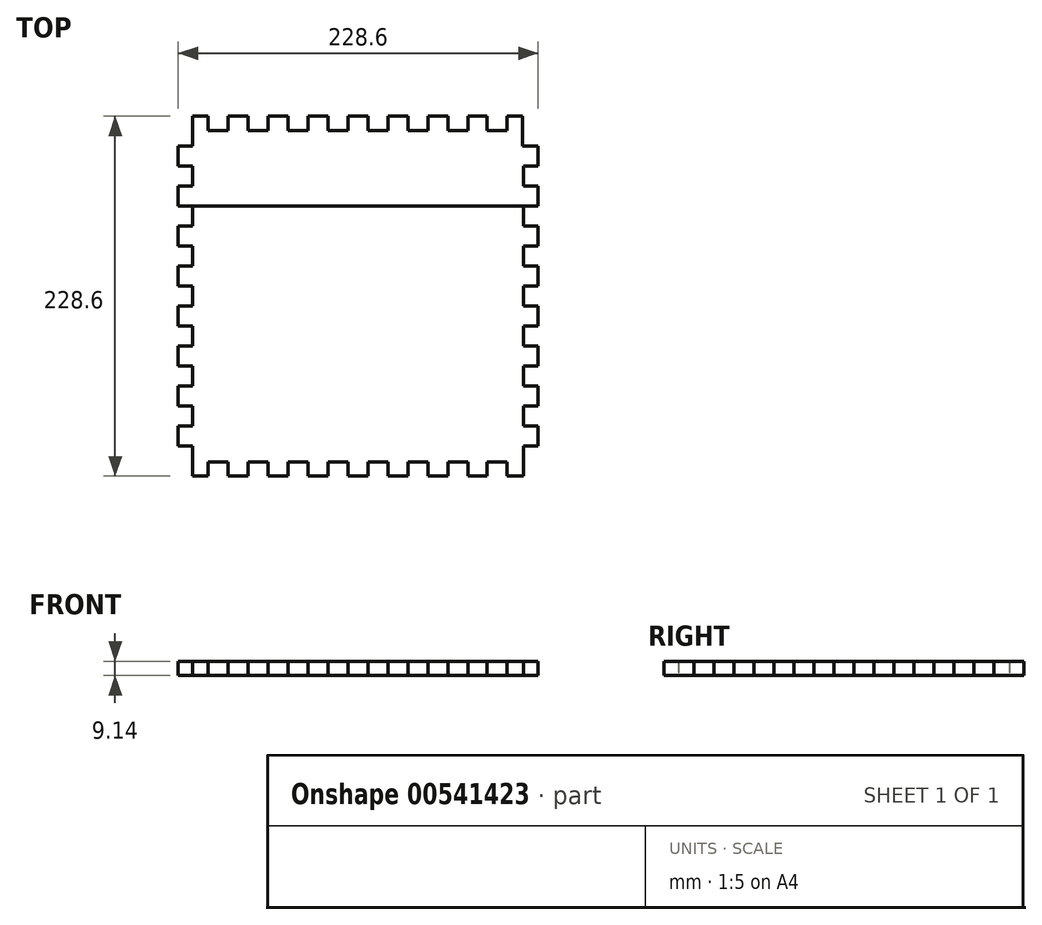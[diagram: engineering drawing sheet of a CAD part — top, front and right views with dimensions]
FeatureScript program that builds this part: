
annotation { "Feature Type Name" : "Feature", "Feature Type Description" : "" }
export const myFeature = defineFeature(function(context is Context, id is Id, definition is map)
    precondition{}
    {
        {
            var Q0;
            Q0=qCreatedBy(makeId("Top.planeOp"),FACE);
            var sketch = newSketch(context, id + "F0", { "sketchPlane" : qUnion([Q0])});
            skLineSegment(sketch, "E0.bottom", {"start": v(9.14, 0) * mm, "end": v(19.05, 0) * mm});
            skLineSegment(sketch, "E0.left", {"start": v(0, -19.05) * mm, "end": v(0, -31.75) * mm});
            skLineSegment(sketch, "E1", {"start": v(9.14, 0) * mm, "end": v(9.14, -19.05) * mm});
            skLineSegment(sketch, "E2", {"start": v(9.14, -19.05) * mm, "end": v(0, -19.05) * mm});
            skPoint(sketch, "E3.orphan", {"position": v(0, 0) * mm});
            skLineSegment(sketch, "E4", {"start": v(19.05, 0) * mm, "end": v(19.05, -9.14) * mm});
            skLineSegment(sketch, "E5", {"start": v(19.05, -9.14) * mm, "end": v(31.75, -9.14) * mm});
            skLineSegment(sketch, "E6", {"start": v(31.75, -9.14) * mm, "end": v(31.75, 0) * mm});
            skLineSegment(sketch, "E7", {"start": v(31.75, 0) * mm, "end": v(44.45, 0) * mm});
            skLineSegment(sketch, "E8", {"start": v(44.45, 0) * mm, "end": v(44.45, -9.14) * mm});
            skLineSegment(sketch, "E9", {"start": v(44.45, -9.14) * mm, "end": v(57.15, -9.14) * mm});
            skLineSegment(sketch, "E10", {"start": v(57.15, -9.14) * mm, "end": v(57.15, 0) * mm});
            skLineSegment(sketch, "E11", {"start": v(57.15, 0) * mm, "end": v(69.85, 0) * mm});
            skLineSegment(sketch, "E12", {"start": v(69.85, 0) * mm, "end": v(69.85, -9.14) * mm});
            skLineSegment(sketch, "E13", {"start": v(69.85, -9.14) * mm, "end": v(82.55, -9.14) * mm});
            skLineSegment(sketch, "E14", {"start": v(82.55, -9.14) * mm, "end": v(82.55, 0) * mm});
            skLineSegment(sketch, "E15", {"start": v(82.55, 0) * mm, "end": v(95.25, 0) * mm});
            skLineSegment(sketch, "E16", {"start": v(95.25, 0) * mm, "end": v(95.25, -9.14) * mm});
            skLineSegment(sketch, "E17", {"start": v(95.25, -9.14) * mm, "end": v(107.95, -9.14) * mm});
            skLineSegment(sketch, "E18", {"start": v(107.95, -9.14) * mm, "end": v(107.95, 0) * mm});
            skLineSegment(sketch, "E19.trimOffspring", {"start": v(107.95, 0) * mm, "end": v(120.65, 0) * mm});
            skLineSegment(sketch, "E20", {"start": v(120.65, 0) * mm, "end": v(120.65, -9.14) * mm});
            skLineSegment(sketch, "E21", {"start": v(120.65, -9.14) * mm, "end": v(133.35, -9.14) * mm});
            skLineSegment(sketch, "E22", {"start": v(133.35, -9.14) * mm, "end": v(133.35, 0) * mm});
            skLineSegment(sketch, "E23", {"start": v(133.35, 0) * mm, "end": v(146.05, 0) * mm});
            skLineSegment(sketch, "E24", {"start": v(146.05, 0) * mm, "end": v(146.05, -9.14) * mm});
            skLineSegment(sketch, "E25", {"start": v(146.05, -9.14) * mm, "end": v(158.75, -9.14) * mm});
            skLineSegment(sketch, "E26", {"start": v(158.75, -9.14) * mm, "end": v(158.75, 0) * mm});
            skLineSegment(sketch, "E27", {"start": v(158.75, 0) * mm, "end": v(171.45, 0) * mm});
            skLineSegment(sketch, "E28", {"start": v(171.45, 0) * mm, "end": v(171.45, -9.14) * mm});
            skLineSegment(sketch, "E29", {"start": v(171.45, -9.14) * mm, "end": v(184.15, -9.14) * mm});
            skLineSegment(sketch, "E30", {"start": v(184.15, -9.14) * mm, "end": v(184.15, 0) * mm});
            skLineSegment(sketch, "E31.trimOffspring", {"start": v(184.15, 0) * mm, "end": v(196.09, 0) * mm});
            skLineSegment(sketch, "E32", {"start": v(196.09, 0) * mm, "end": v(196.09, -9.14) * mm});
            skLineSegment(sketch, "E33", {"start": v(196.09, -9.14) * mm, "end": v(208.79, -9.14) * mm});
            skLineSegment(sketch, "E34", {"start": v(208.79, -9.14) * mm, "end": v(208.79, 0) * mm});
            skLineSegment(sketch, "E35.trimOffspring", {"start": v(208.79, 0) * mm, "end": v(218.7, 0) * mm});
            skLineSegment(sketch, "E36", {"start": v(218.7, 0) * mm, "end": v(218.7, -19.05) * mm});
            skLineSegment(sketch, "E37", {"start": v(218.7, -19.05) * mm, "end": v(228.6, -19.05) * mm});
            skPoint(sketch, "E38.orphan", {"position": v(228.6, 0) * mm});
            skLineSegment(sketch, "E39", {"start": v(0, -31.75) * mm, "end": v(9.14, -31.75) * mm});
            skLineSegment(sketch, "E40", {"start": v(9.14, -31.75) * mm, "end": v(9.14, -44.45) * mm});
            skLineSegment(sketch, "E41", {"start": v(9.14, -44.45) * mm, "end": v(0, -44.45) * mm});
            skLineSegment(sketch, "E42", {"start": v(0, -44.45) * mm, "end": v(0, -57.15) * mm});
            skLineSegment(sketch, "E43", {"start": v(0, -57.15) * mm, "end": v(9.14, -57.15) * mm});
            skLineSegment(sketch, "E44", {"start": v(9.14, -57.15) * mm, "end": v(9.14, -69.85) * mm});
            skLineSegment(sketch, "E45", {"start": v(9.14, -69.85) * mm, "end": v(0, -69.85) * mm});
            skLineSegment(sketch, "E46", {"start": v(0, -69.85) * mm, "end": v(0, -82.55) * mm});
            skLineSegment(sketch, "E47", {"start": v(0, -82.55) * mm, "end": v(9.14, -82.55) * mm});
            skLineSegment(sketch, "E48", {"start": v(9.14, -82.55) * mm, "end": v(9.14, -95.25) * mm});
            skLineSegment(sketch, "E49", {"start": v(9.14, -95.25) * mm, "end": v(0, -95.25) * mm});
            skLineSegment(sketch, "E50", {"start": v(0, -95.25) * mm, "end": v(0, -107.95) * mm});
            skLineSegment(sketch, "E51", {"start": v(0, -107.95) * mm, "end": v(9.14, -107.95) * mm});
            skLineSegment(sketch, "E52", {"start": v(9.14, -107.95) * mm, "end": v(9.14, -120.65) * mm});
            skLineSegment(sketch, "E53", {"start": v(9.14, -120.65) * mm, "end": v(0, -120.65) * mm});
            skLineSegment(sketch, "E54.trimOffspring", {"start": v(0, -120.65) * mm, "end": v(0, -133.35) * mm});
            skLineSegment(sketch, "E55", {"start": v(0, -133.35) * mm, "end": v(9.14, -133.35) * mm});
            skLineSegment(sketch, "E56", {"start": v(9.14, -133.35) * mm, "end": v(9.14, -146.05) * mm});
            skLineSegment(sketch, "E57", {"start": v(9.14, -146.05) * mm, "end": v(0, -146.05) * mm});
            skLineSegment(sketch, "E58", {"start": v(0, -146.05) * mm, "end": v(0, -158.75) * mm});
            skLineSegment(sketch, "E59", {"start": v(0, -158.75) * mm, "end": v(9.14, -158.75) * mm});
            skLineSegment(sketch, "E60", {"start": v(9.14, -158.75) * mm, "end": v(9.14, -171.45) * mm});
            skLineSegment(sketch, "E61", {"start": v(9.14, -171.45) * mm, "end": v(0, -171.45) * mm});
            skLineSegment(sketch, "E62", {"start": v(0, -171.45) * mm, "end": v(0, -184.15) * mm});
            skLineSegment(sketch, "E63", {"start": v(0, -184.15) * mm, "end": v(9.14, -184.15) * mm});
            skLineSegment(sketch, "E64", {"start": v(9.14, -184.15) * mm, "end": v(9.14, -196.85) * mm});
            skLineSegment(sketch, "E65", {"start": v(9.14, -196.85) * mm, "end": v(0, -196.85) * mm});
            skLineSegment(sketch, "E66.trimOffspring", {"start": v(0, -196.85) * mm, "end": v(0, -209.55) * mm});
            skLineSegment(sketch, "E67", {"start": v(0, -209.55) * mm, "end": v(9.14, -209.55) * mm});
            skLineSegment(sketch, "E68", {"start": v(9.14, -209.55) * mm, "end": v(9.14, -228.6) * mm});
            skPoint(sketch, "E69.orphan", {"position": v(0, -228.6) * mm});
            skLineSegment(sketch, "E70", {"start": v(114.3, 0) * mm, "end": v(114.3, -44.1) * mm, "construction": true});
            skLineSegment(sketch, "E71", {"start": v(9.14, -114.3) * mm, "end": v(76.5, -114.3) * mm, "construction": true});
            skLineSegment(sketch, "E72.MirrorCS", {"start": v(228.6, -19.05) * mm, "end": v(228.6, -31.75) * mm});
            skLineSegment(sketch, "E73.MirrorCS", {"start": v(228.6, -31.75) * mm, "end": v(219.46, -31.75) * mm});
            skLineSegment(sketch, "E74.MirrorCS", {"start": v(219.46, -31.75) * mm, "end": v(219.46, -44.45) * mm});
            skLineSegment(sketch, "E75.MirrorCS", {"start": v(219.46, -44.45) * mm, "end": v(228.6, -44.45) * mm});
            skLineSegment(sketch, "E76.MirrorCS", {"start": v(228.6, -44.45) * mm, "end": v(228.6, -57.15) * mm});
            skLineSegment(sketch, "E77.MirrorCS", {"start": v(228.6, -57.15) * mm, "end": v(219.46, -57.15) * mm});
            skLineSegment(sketch, "E78.MirrorCS", {"start": v(219.46, -57.15) * mm, "end": v(219.46, -69.85) * mm});
            skLineSegment(sketch, "E79.MirrorCS", {"start": v(219.46, -69.85) * mm, "end": v(228.6, -69.85) * mm});
            skLineSegment(sketch, "E80.MirrorCS", {"start": v(228.6, -69.85) * mm, "end": v(228.6, -82.55) * mm});
            skLineSegment(sketch, "E81.MirrorCS", {"start": v(228.6, -82.55) * mm, "end": v(219.46, -82.55) * mm});
            skLineSegment(sketch, "E82.MirrorCS", {"start": v(219.46, -82.55) * mm, "end": v(219.46, -95.25) * mm});
            skLineSegment(sketch, "E83.MirrorCS", {"start": v(219.46, -95.25) * mm, "end": v(228.6, -95.25) * mm});
            skLineSegment(sketch, "E84.MirrorCS", {"start": v(228.6, -95.25) * mm, "end": v(228.6, -107.95) * mm});
            skLineSegment(sketch, "E85.MirrorCS", {"start": v(228.6, -107.95) * mm, "end": v(219.46, -107.95) * mm});
            skLineSegment(sketch, "E86.MirrorCS", {"start": v(219.46, -107.95) * mm, "end": v(219.46, -120.65) * mm});
            skLineSegment(sketch, "E87.MirrorCS", {"start": v(219.46, -120.65) * mm, "end": v(228.6, -120.65) * mm});
            skLineSegment(sketch, "E88.MirrorCS", {"start": v(228.6, -120.65) * mm, "end": v(228.6, -133.35) * mm});
            skLineSegment(sketch, "E89.MirrorCS", {"start": v(228.6, -133.35) * mm, "end": v(219.46, -133.35) * mm});
            skLineSegment(sketch, "E90.MirrorCS", {"start": v(219.46, -133.35) * mm, "end": v(219.46, -146.05) * mm});
            skLineSegment(sketch, "E91.MirrorCS", {"start": v(219.46, -146.05) * mm, "end": v(228.6, -146.05) * mm});
            skLineSegment(sketch, "E92.MirrorCS", {"start": v(228.6, -146.05) * mm, "end": v(228.6, -158.75) * mm});
            skLineSegment(sketch, "E93.MirrorCS", {"start": v(228.6, -158.75) * mm, "end": v(219.46, -158.75) * mm});
            skLineSegment(sketch, "E94.MirrorCS", {"start": v(219.46, -158.75) * mm, "end": v(219.46, -171.45) * mm});
            skLineSegment(sketch, "E95.MirrorCS", {"start": v(219.46, -171.45) * mm, "end": v(228.6, -171.45) * mm});
            skLineSegment(sketch, "E96.MirrorCS", {"start": v(228.6, -171.45) * mm, "end": v(228.6, -184.15) * mm});
            skLineSegment(sketch, "E97.MirrorCS", {"start": v(228.6, -184.15) * mm, "end": v(219.46, -184.15) * mm});
            skLineSegment(sketch, "E98.MirrorCS", {"start": v(219.46, -184.15) * mm, "end": v(219.46, -196.85) * mm});
            skLineSegment(sketch, "E99.MirrorCS", {"start": v(219.46, -196.85) * mm, "end": v(228.6, -196.85) * mm});
            skLineSegment(sketch, "E100.MirrorCS", {"start": v(228.6, -196.85) * mm, "end": v(228.6, -209.55) * mm});
            skLineSegment(sketch, "E101.MirrorCS", {"start": v(228.6, -209.55) * mm, "end": v(219.46, -209.55) * mm});
            skLineSegment(sketch, "E102.MirrorCS", {"start": v(219.46, -209.55) * mm, "end": v(219.46, -228.6) * mm});
            skLineSegment(sketch, "E103.MirrorCS", {"start": v(9.14, -228.6) * mm, "end": v(19.05, -228.6) * mm});
            skLineSegment(sketch, "E104.MirrorCS", {"start": v(19.05, -228.6) * mm, "end": v(19.05, -219.46) * mm});
            skLineSegment(sketch, "E105.MirrorCS", {"start": v(19.05, -219.46) * mm, "end": v(31.75, -219.46) * mm});
            skLineSegment(sketch, "E106.MirrorCS", {"start": v(31.75, -219.46) * mm, "end": v(31.75, -228.6) * mm});
            skLineSegment(sketch, "E107.MirrorCS", {"start": v(31.75, -228.6) * mm, "end": v(44.45, -228.6) * mm});
            skLineSegment(sketch, "E108.MirrorCS", {"start": v(44.45, -228.6) * mm, "end": v(44.45, -219.46) * mm});
            skLineSegment(sketch, "E109.MirrorCS", {"start": v(44.45, -219.46) * mm, "end": v(57.15, -219.46) * mm});
            skLineSegment(sketch, "E110.MirrorCS", {"start": v(57.15, -219.46) * mm, "end": v(57.15, -228.6) * mm});
            skLineSegment(sketch, "E111.MirrorCS", {"start": v(57.15, -228.6) * mm, "end": v(69.85, -228.6) * mm});
            skLineSegment(sketch, "E112.MirrorCS", {"start": v(69.85, -228.6) * mm, "end": v(69.85, -219.46) * mm});
            skLineSegment(sketch, "E113.MirrorCS", {"start": v(69.85, -219.46) * mm, "end": v(82.55, -219.46) * mm});
            skLineSegment(sketch, "E114.MirrorCS", {"start": v(82.55, -219.46) * mm, "end": v(82.55, -228.6) * mm});
            skLineSegment(sketch, "E115.MirrorCS", {"start": v(82.55, -228.6) * mm, "end": v(95.25, -228.6) * mm});
            skLineSegment(sketch, "E116.MirrorCS", {"start": v(95.25, -228.6) * mm, "end": v(95.25, -219.46) * mm});
            skLineSegment(sketch, "E117.MirrorCS", {"start": v(95.25, -219.46) * mm, "end": v(107.95, -219.46) * mm});
            skLineSegment(sketch, "E118.MirrorCS", {"start": v(107.95, -219.46) * mm, "end": v(107.95, -228.6) * mm});
            skLineSegment(sketch, "E119.MirrorCS", {"start": v(107.95, -228.6) * mm, "end": v(120.65, -228.6) * mm});
            skLineSegment(sketch, "E120.MirrorCS", {"start": v(120.65, -228.6) * mm, "end": v(120.65, -219.46) * mm});
            skLineSegment(sketch, "E121.MirrorCS", {"start": v(120.65, -219.46) * mm, "end": v(133.35, -219.46) * mm});
            skLineSegment(sketch, "E122.MirrorCS", {"start": v(133.35, -219.46) * mm, "end": v(133.35, -228.6) * mm});
            skLineSegment(sketch, "E123.MirrorCS", {"start": v(133.35, -228.6) * mm, "end": v(146.05, -228.6) * mm});
            skLineSegment(sketch, "E124.MirrorCS", {"start": v(146.05, -228.6) * mm, "end": v(146.05, -219.46) * mm});
            skLineSegment(sketch, "E125.MirrorCS", {"start": v(146.05, -219.46) * mm, "end": v(158.75, -219.46) * mm});
            skLineSegment(sketch, "E126.MirrorCS", {"start": v(158.75, -219.46) * mm, "end": v(158.75, -228.6) * mm});
            skLineSegment(sketch, "E127.MirrorCS", {"start": v(158.75, -228.6) * mm, "end": v(171.45, -228.6) * mm});
            skLineSegment(sketch, "E128.MirrorCS", {"start": v(171.45, -228.6) * mm, "end": v(171.45, -219.46) * mm});
            skLineSegment(sketch, "E129.MirrorCS", {"start": v(171.45, -219.46) * mm, "end": v(184.15, -219.46) * mm});
            skLineSegment(sketch, "E130.MirrorCS", {"start": v(184.15, -219.46) * mm, "end": v(184.15, -228.6) * mm});
            skLineSegment(sketch, "E131.MirrorCS", {"start": v(184.15, -228.6) * mm, "end": v(196.09, -228.6) * mm});
            skLineSegment(sketch, "E132.MirrorCS", {"start": v(196.09, -228.6) * mm, "end": v(196.09, -219.46) * mm});
            skLineSegment(sketch, "E133.MirrorCS", {"start": v(196.09, -219.46) * mm, "end": v(208.79, -219.46) * mm});
            skLineSegment(sketch, "E134.MirrorCS", {"start": v(208.79, -219.46) * mm, "end": v(208.79, -228.6) * mm});
            skLineSegment(sketch, "E135", {"start": v(9.14, -57.15) * mm, "end": v(219.46, -57.15) * mm});
            skLineSegment(sketch, "E136", {"start": v(208.79, -228.6) * mm, "end": v(219.46, -228.6) * mm});
            skSolve(sketch);
        }
        {
            var Q0;
            Q0=makeQuery(id+"F0.imprint","IMPRINT",FACE,{"disambiguationData":[TD([[makeQuery(id+"F0.imprint","IMPRINT",EDGE,{"derivedFrom":sQuery(id+"F0.wireOp",EDGE,"E1")}),1.0]])]});
            extrude(context, id + "F1", {"entities" : qUnion([Q0]), "depth" : 9.14 * mm, "offsetDistance" : 25.4 * mm});
        }
        {
            var Q0;
            Q0=makeQuery(id+"F0.imprint","IMPRINT",FACE,{"disambiguationData":[TD([[makeQuery(id+"F0.imprint","IMPRINT",EDGE,{"derivedFrom":sQuery(id+"F0.wireOp",EDGE,"E44")}),1.0]])]});
            extrude(context, id + "F2", {"entities" : qUnion([Q0]), "depth" : 9.14 * mm, "offsetDistance" : 25.4 * mm});
        }
    });
